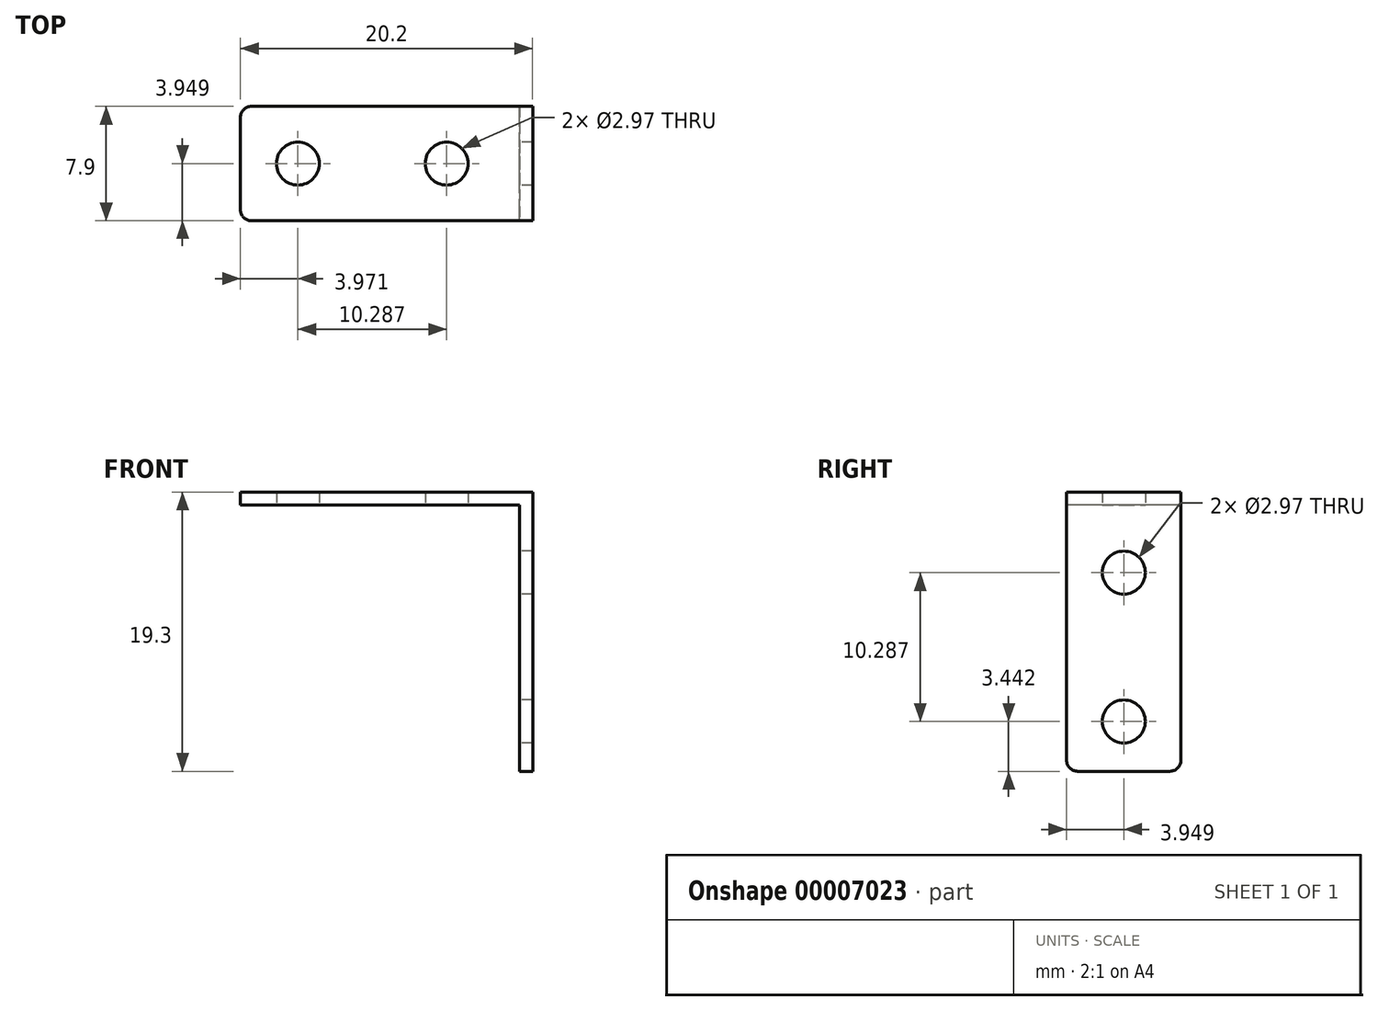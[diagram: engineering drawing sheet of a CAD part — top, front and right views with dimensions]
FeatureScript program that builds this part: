
annotation { "Feature Type Name" : "Feature", "Feature Type Description" : "" }
export const myFeature = defineFeature(function(context is Context, id is Id, definition is map)
    precondition{}
    {
        {
            var Q0;
            Q0=qCreatedBy(makeId("Top.planeOp"),FACE);
            var sketch = newSketch(context, id + "F0", { "sketchPlane" : qUnion([Q0])});
            skLineSegment(sketch, "E0.bottom", {"start": v(-58.17, -9.46) * mm, "end": v(-38.87, -9.46) * mm});
            skLineSegment(sketch, "E0.top", {"start": v(-58.17, -17.36) * mm, "end": v(-38.87, -17.36) * mm});
            skLineSegment(sketch, "E0.left", {"start": v(-58.17, -9.46) * mm, "end": v(-58.17, -17.36) * mm});
            skLineSegment(sketch, "E0.right", {"start": v(-38.87, -9.46) * mm, "end": v(-38.87, -17.36) * mm});
            skSolve(sketch);
        }
        {
            var Q0;
            Q0 = qSketchRegion(id + "F0", true);
            extrude(context, id + "F1", {"entities" : qUnion([Q0]), "depth" : 0.91 * mm});
        }
        {
            var Q0;
            Q0=makeQuery(id+"F1.opExtrude","CAP_FACE",FACE,{"disambiguationData":[OSD([sQuery(id+"F0.wireOp",EDGE,"E0.bottom"),sQuery(id+"F0.wireOp",EDGE,"E0.top"),sQuery(id+"F0.wireOp",EDGE,"E0.left"),sQuery(id+"F0.wireOp",EDGE,"E0.right")])],"isStart":true});
            var sketch = newSketch(context, id + "F2", { "sketchPlane" : qUnion([Q0])});
            skCircle(sketch, "E1", {"center": v(-54.2, 13.41) * mm, "radius": 1.49 * mm});
            skCircle(sketch, "E2.1.0.0", {"center": v(-43.91, 13.41) * mm, "radius": 1.49 * mm});
            skLineSegment(sketch, "E2.direction1", {"start": v(-54.2, 13.41) * mm, "end": v(-43.91, 13.41) * mm, "construction": true});
            skLineSegment(sketch, "E3", {"start": v(-43.91, 17.36) * mm, "end": v(-43.91, 9.46) * mm, "construction": true});
            skSolve(sketch);
        }
        {
            var Q0;
            Q0 = qSketchRegion(id + "F2", true);
            extrude(context, id + "F3", {"entities" : qUnion([Q0]), "operationType" : NewBodyOperationType.REMOVE, "oppositeDirection" : true, "depth" : 25.4 * mm});
        }
        {
            var Q0;
            Q0=makeQuery(id+"F1.opExtrude","SWEPT_FACE",FACE,{"disambiguationData":[OSD([sQuery(id+"F0.wireOp",EDGE,"E0.right")])]});
            var sketch = newSketch(context, id + "F4", { "sketchPlane" : qUnion([Q0])});
            skLineSegment(sketch, "E4.bottom", {"start": v(-17.36, 0.91) * mm, "end": v(-9.46, 0.91) * mm});
            skLineSegment(sketch, "E4.top", {"start": v(-17.36, -18.39) * mm, "end": v(-9.46, -18.39) * mm});
            skLineSegment(sketch, "E4.left", {"start": v(-17.36, 0.91) * mm, "end": v(-17.36, -18.39) * mm});
            skLineSegment(sketch, "E4.right", {"start": v(-9.46, 0.91) * mm, "end": v(-9.46, -18.39) * mm});
            skSolve(sketch);
        }
        {
            var Q0;
            Q0 = qSketchRegion(id + "F4", true);
            extrude(context, id + "F5", {"entities" : qUnion([Q0]), "operationType" : NewBodyOperationType.ADD, "depth" : 0.9 * mm});
        }
        {
            var Q0;
            Q0=makeQuery(id+"F5.opExtrude","CAP_FACE",FACE,{"disambiguationData":[OSD([sQuery(id+"F4.wireOp",EDGE,"E4.bottom"),sQuery(id+"F4.wireOp",EDGE,"E4.top"),sQuery(id+"F4.wireOp",EDGE,"E4.left"),sQuery(id+"F4.wireOp",EDGE,"E4.right")])],"isStart":true});
            var sketch = newSketch(context, id + "F6", { "sketchPlane" : qUnion([Q0])});
            skCircle(sketch, "E5", {"center": v(13.41, -4.66) * mm, "radius": 1.49 * mm});
            skLineSegment(sketch, "E6", {"start": v(17.36, -4.66) * mm, "end": v(9.46, -4.66) * mm, "construction": true});
            skCircle(sketch, "E7.0.1.0", {"center": v(13.41, -14.95) * mm, "radius": 1.49 * mm});
            skLineSegment(sketch, "E7.direction2", {"start": v(13.41, -4.66) * mm, "end": v(13.41, -14.95) * mm, "construction": true});
            skSolve(sketch);
        }
        {
            var Q0;
            Q0 = qSketchRegion(id + "F6", true);
            extrude(context, id + "F7", {"entities" : qUnion([Q0]), "operationType" : NewBodyOperationType.REMOVE, "oppositeDirection" : true, "depth" : 25.4 * mm});
        }
        {
            var Q0;
            Q0=makeQuery(id+"F1.opExtrude","SWEPT_EDGE",EDGE,{"disambiguationData":[OSD([sQuery(id+"F0.wireOp",EDGE,"E0.top"),sQuery(id+"F0.wireOp",EDGE,"E0.left")])]});
            var Q1;
            Q1=makeQuery(id+"F1.opExtrude","SWEPT_EDGE",EDGE,{"disambiguationData":[OSD([sQuery(id+"F0.wireOp",EDGE,"E0.bottom"),sQuery(id+"F0.wireOp",EDGE,"E0.left")])]});
            var Q2;
            Q2=makeQuery(id+"F5.opExtrude","SWEPT_EDGE",EDGE,{"disambiguationData":[OSD([sQuery(id+"F4.wireOp",EDGE,"E4.top"),sQuery(id+"F4.wireOp",EDGE,"E4.left")])]});
            var Q3;
            Q3=makeQuery(id+"F5.opExtrude","SWEPT_EDGE",EDGE,{"disambiguationData":[OSD([sQuery(id+"F4.wireOp",EDGE,"E4.top"),sQuery(id+"F4.wireOp",EDGE,"E4.right")])]});
            fillet(context, id + "F8", {"entities" : qUnion([Q0, Q1, Q2, Q3]), "radius" : 0.76 * mm, "tangentPropagation" : true, "allowEdgeOverflow" : false});
        }
    });
